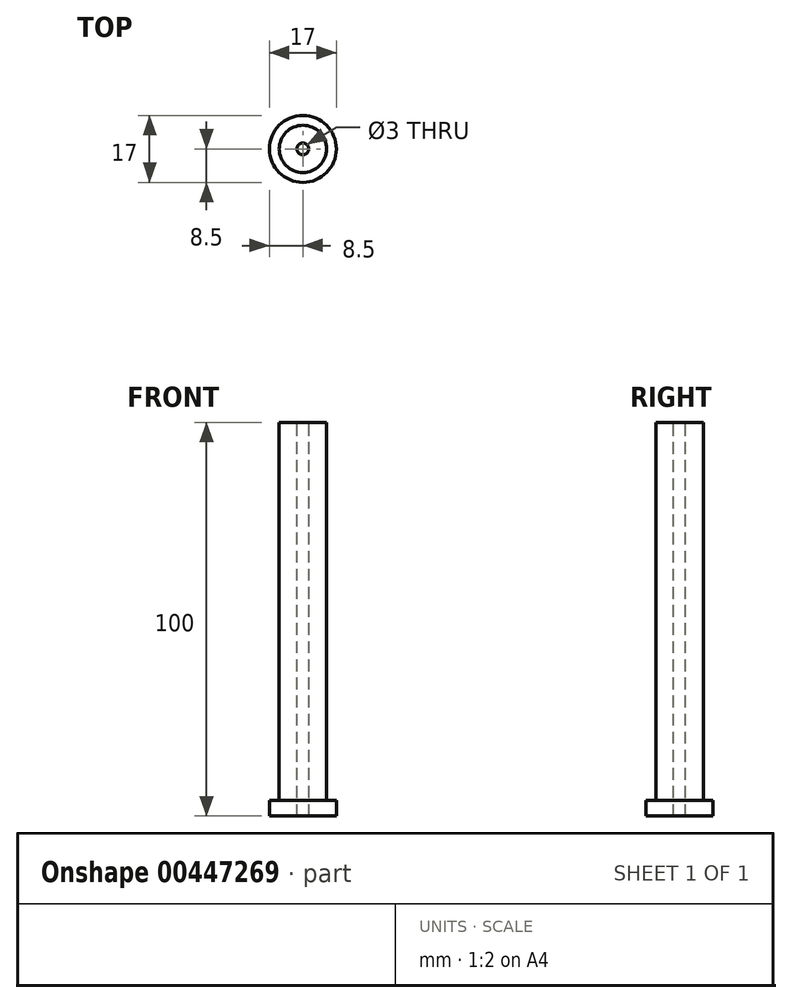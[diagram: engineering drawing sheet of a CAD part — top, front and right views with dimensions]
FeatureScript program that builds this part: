
annotation { "Feature Type Name" : "Feature", "Feature Type Description" : "" }
export const myFeature = defineFeature(function(context is Context, id is Id, definition is map)
    precondition{}
    {
        {
            var Q0;
            Q0=qCreatedBy(makeId("Top.planeOp"),FACE);
            var sketch = newSketch(context, id + "F0", { "sketchPlane" : qUnion([Q0])});
            skCircle(sketch, "E0", {"center": v(0, 0) * mm, "radius": 8.5 * mm});
            skSolve(sketch);
        }
        {
            var Q0;
            Q0=qSketchRegion(id+"F0",true);
            extrude(context, id + "F1", {"entities" : qUnion([Q0]), "depth" : 4 * mm});
        }
        {
            var Q0;
            Q0=qCreatedBy(makeId("Top.planeOp"),FACE);
            var sketch = newSketch(context, id + "F2", { "sketchPlane" : qUnion([Q0])});
            skCircle(sketch, "E1", {"center": v(0, 0) * mm, "radius": 6 * mm});
            skSolve(sketch);
        }
        {
            var Q0;
            Q0=qSketchRegion(id+"F2",true);
            extrude(context, id + "F3", {"entities" : qUnion([Q0]), "operationType" : NewBodyOperationType.ADD, "depth" : 100 * mm});
        }
        {
            var Q0;
            Q0=makeQuery(id+"F3.opExtrude","CAP_FACE",FACE,{"disambiguationData":[OSD([sQuery(id+"F2.wireOp",EDGE,"E1")])],"isStart":false});
            var sketch = newSketch(context, id + "F4", { "sketchPlane" : qUnion([Q0])});
            skCircle(sketch, "E2", {"center": v(0, 0) * mm, "radius": 1.5 * mm});
            skSolve(sketch);
        }
        {
            var Q0;
            Q0=makeQuery(id+"F4.imprint","IMPRINT",FACE,{"disambiguationData":[TD([[makeQuery(id+"F4.imprint","IMPRINT",EDGE,{"derivedFrom":sQuery(id+"F4.wireOp",EDGE,"E2")}),1.0]])]});
            extrude(context, id + "F5", {"entities" : qUnion([Q0]), "operationType" : NewBodyOperationType.REMOVE, "oppositeDirection" : true, "depth" : 114.9 * mm});
        }
    });
